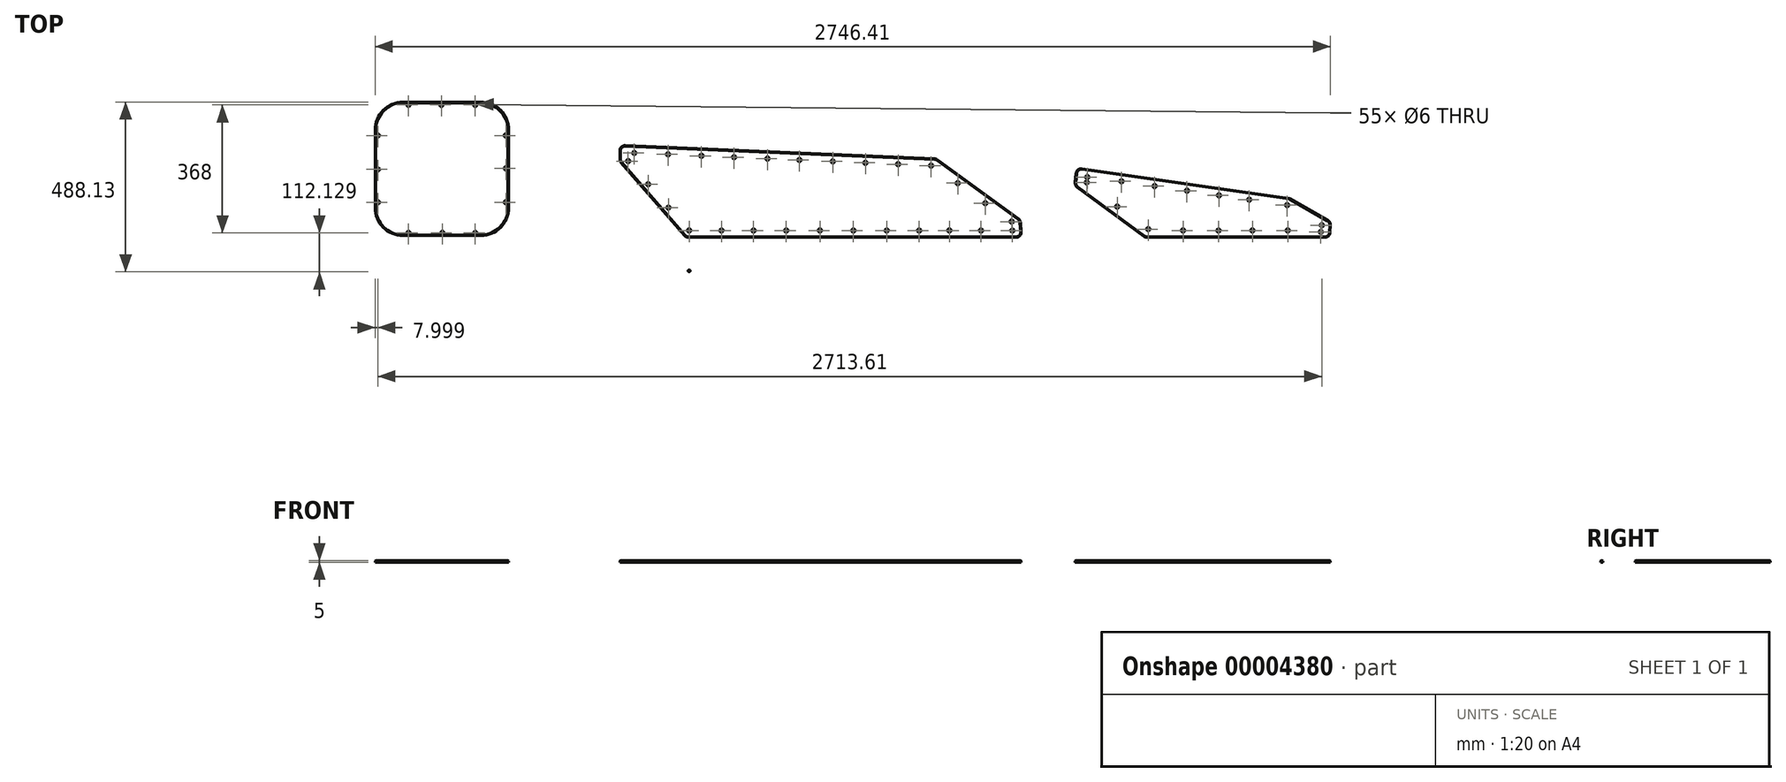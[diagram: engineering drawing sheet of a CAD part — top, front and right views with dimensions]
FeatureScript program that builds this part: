
annotation { "Feature Type Name" : "Feature", "Feature Type Description" : "" }
export const myFeature = defineFeature(function(context is Context, id is Id, definition is map)
    precondition{}
    {
        {
            var Q0;
            Q0=qCreatedBy(makeId("Top.planeOp"),FACE);
            var sketch = newSketch(context, id + "F0", { "sketchPlane" : qUnion([Q0])});
            skLineSegment(sketch, "E0", {"start": v(-249.6, -64.7) * mm, "end": v(262.12, -64.7) * mm});
            skLineSegment(sketch, "E1", {"start": v(277.1, -50.37) * mm, "end": v(278.06, -28.88) * mm});
            skLineSegment(sketch, "E2", {"start": v(270.54, -15.2) * mm, "end": v(163.96, 45.87) * mm});
            skLineSegment(sketch, "E3", {"start": v(158.63, 47.7) * mm, "end": v(-436, 133.07) * mm});
            skLineSegment(sketch, "E4", {"start": v(-453.05, 119.68) * mm, "end": v(-455.69, 92.78) * mm});
            skLineSegment(sketch, "E5", {"start": v(-449.66, 79.24) * mm, "end": v(-258.5, -61.77) * mm});
            skCircle(sketch, "E6", {"center": v(-420.96, 108.82) * mm, "radius": 3 * mm});
            skCircle(sketch, "E7", {"center": v(-422.47, 93.47) * mm, "radius": 3 * mm});
            skCircle(sketch, "E8", {"center": v(-322.71, 96.71) * mm, "radius": 3 * mm});
            skCircle(sketch, "E9", {"center": v(-334.84, 23.85) * mm, "radius": 3 * mm});
            skCircle(sketch, "E10", {"center": v(-245.64, -40.7) * mm, "radius": 3 * mm});
            skCircle(sketch, "E11", {"center": v(-145.53, -44.7) * mm, "radius": 3 * mm});
            skCircle(sketch, "E12", {"center": v(-43.53, -44.7) * mm, "radius": 3 * mm});
            skCircle(sketch, "E13", {"center": v(53.97, -44.7) * mm, "radius": 3 * mm});
            skCircle(sketch, "E14", {"center": v(155.47, -44.7) * mm, "radius": 3 * mm});
            skCircle(sketch, "E15", {"center": v(250.47, -48.7) * mm, "radius": 3 * mm});
            skCircle(sketch, "E16", {"center": v(253.28, -29.52) * mm, "radius": 3 * mm});
            skCircle(sketch, "E17", {"center": v(153.67, 28.21) * mm, "radius": 3 * mm});
            skCircle(sketch, "E18", {"center": v(44.8, 43.87) * mm, "radius": 3 * mm});
            skCircle(sketch, "E19", {"center": v(-42.3, 56.4) * mm, "radius": 3 * mm});
            skCircle(sketch, "E20", {"center": v(-134.36, 69.63) * mm, "radius": 3 * mm});
            skCircle(sketch, "E21", {"center": v(-227.4, 83) * mm, "radius": 3 * mm});
            skLineSegment(sketch, "E22", {"start": v(-625.64, -64.7) * mm, "end": v(-1567.54, -64.7) * mm});
            skLineSegment(sketch, "E23", {"start": v(-1578.88, -59.52) * mm, "end": v(-1761.2, 151.07) * mm});
            skLineSegment(sketch, "E24", {"start": v(-1764.87, 160.89) * mm, "end": v(-1764.87, 184.64) * mm});
            skLineSegment(sketch, "E25", {"start": v(-1749.23, 199.63) * mm, "end": v(-859.52, 161.5) * mm});
            skLineSegment(sketch, "E26", {"start": v(-851.32, 158.63) * mm, "end": v(-618.96, -10.8) * mm});
            skLineSegment(sketch, "E27", {"start": v(-612.84, -21.73) * mm, "end": v(-610.7, -48.5) * mm});
            skLineSegment(sketch, "E28", {"start": v(-613.21, -17.1) * mm, "end": v(-613.95, -17.16) * mm});
            skCircle(sketch, "E29", {"center": v(-1723.05, 178.36) * mm, "radius": 3 * mm});
            skCircle(sketch, "E30", {"center": v(-1740.97, 154.78) * mm, "radius": 3 * mm});
            skCircle(sketch, "E31", {"center": v(-1683.36, 88.25) * mm, "radius": 3 * mm});
            skCircle(sketch, "E32", {"center": v(-1626.14, 174.22) * mm, "radius": 3 * mm});
            skCircle(sketch, "E33", {"center": v(-1530.23, 170.13) * mm, "radius": 3 * mm});
            skCircle(sketch, "E34", {"center": v(-1436.31, 166.11) * mm, "radius": 3 * mm});
            skCircle(sketch, "E35", {"center": v(-1625.1, 20.97) * mm, "radius": 3 * mm});
            skCircle(sketch, "E36", {"center": v(-1565.4, -44.7) * mm, "radius": 3 * mm});
            skCircle(sketch, "E37", {"center": v(-1472.4, -44.7) * mm, "radius": 3 * mm});
            skCircle(sketch, "E38", {"center": v(-1380.4, -44.7) * mm, "radius": 3 * mm});
            skCircle(sketch, "E39", {"center": v(-1340.4, 162.02) * mm, "radius": 3 * mm});
            skCircle(sketch, "E40", {"center": v(-1248.48, 158.1) * mm, "radius": 3 * mm});
            skCircle(sketch, "E41", {"center": v(-1286.4, -44.7) * mm, "radius": 3 * mm});
            skCircle(sketch, "E42", {"center": v(-1189.4, -44.7) * mm, "radius": 3 * mm});
            skCircle(sketch, "E43", {"center": v(-1152.57, 154) * mm, "radius": 3 * mm});
            skCircle(sketch, "E44", {"center": v(-1058.66, 149.98) * mm, "radius": 3 * mm});
            skCircle(sketch, "E45", {"center": v(-1093.4, -44.7) * mm, "radius": 3 * mm});
            skCircle(sketch, "E46", {"center": v(-997.4, -44.7) * mm, "radius": 3 * mm});
            skCircle(sketch, "E47", {"center": v(-964.74, 145.97) * mm, "radius": 3 * mm});
            skCircle(sketch, "E48", {"center": v(-869.83, 141.91) * mm, "radius": 3 * mm});
            skCircle(sketch, "E49", {"center": v(-904.4, -44.7) * mm, "radius": 3 * mm});
            skCircle(sketch, "E50", {"center": v(-793.24, 91.52) * mm, "radius": 3 * mm});
            skCircle(sketch, "E51", {"center": v(-817.4, -44.7) * mm, "radius": 3 * mm});
            skCircle(sketch, "E52", {"center": v(-714.06, 33.79) * mm, "radius": 3 * mm});
            skCircle(sketch, "E53", {"center": v(-726.4, -44.7) * mm, "radius": 3 * mm});
            skCircle(sketch, "E54", {"center": v(-638.13, -19.1) * mm, "radius": 3 * mm});
            skCircle(sketch, "E55", {"center": v(-636.4, -44.7) * mm, "radius": 3 * mm});
            skPoint(sketch, "E56.visualSharp", {"position": v(-1574.4, -64.7) * mm});
            skArc(sketch, "E56.filletArc", {"start": v(-1578.88, -59.52) * mm, "mid": v(-1573.77, -63.35) * mm, "end": v(-1567.54, -64.7) * mm});
            skPoint(sketch, "E57.visualSharp", {"position": v(-1764.87, 155.3) * mm});
            skArc(sketch, "E57.filletArc", {"start": v(-1764.87, 160.89) * mm, "mid": v(-1763.92, 155.65) * mm, "end": v(-1761.2, 151.07) * mm});
            skPoint(sketch, "E58.visualSharp", {"position": v(-1764.87, 200.3) * mm});
            skArc(sketch, "E58.filletArc", {"start": v(-1749.23, 199.63) * mm, "mid": v(-1760.24, 195.47) * mm, "end": v(-1764.87, 184.64) * mm});
            skPoint(sketch, "E59.visualSharp", {"position": v(-854.99, 161.3) * mm});
            skArc(sketch, "E59.filletArc", {"start": v(-851.32, 158.63) * mm, "mid": v(-855.2, 160.66) * mm, "end": v(-859.52, 161.5) * mm});
            skPoint(sketch, "E60.visualSharp", {"position": v(-613.4, -14.86) * mm});
            skArc(sketch, "E60.filletArc", {"start": v(-612.84, -21.73) * mm, "mid": v(-614.7, -15.6) * mm, "end": v(-618.96, -10.8) * mm});
            skPoint(sketch, "E61.visualSharp", {"position": v(-609.4, -64.7) * mm});
            skArc(sketch, "E61.filletArc", {"start": v(-625.64, -64.7) * mm, "mid": v(-614.62, -59.88) * mm, "end": v(-610.7, -48.5) * mm});
            skPoint(sketch, "E62.visualSharp", {"position": v(-451.52, 135.3) * mm});
            skArc(sketch, "E62.filletArc", {"start": v(-436, 133.07) * mm, "mid": v(-447.38, 130.02) * mm, "end": v(-453.05, 119.68) * mm});
            skPoint(sketch, "E63.visualSharp", {"position": v(-456.52, 84.3) * mm});
            skArc(sketch, "E63.filletArc", {"start": v(-455.69, 92.78) * mm, "mid": v(-454.46, 85.21) * mm, "end": v(-449.66, 79.24) * mm});
            skPoint(sketch, "E64.visualSharp", {"position": v(-254.53, -64.7) * mm});
            skArc(sketch, "E64.filletArc", {"start": v(-258.5, -61.77) * mm, "mid": v(-254.28, -63.95) * mm, "end": v(-249.6, -64.7) * mm});
            skPoint(sketch, "E65.visualSharp", {"position": v(276.47, -64.7) * mm});
            skArc(sketch, "E65.filletArc", {"start": v(262.12, -64.7) * mm, "mid": v(272.5, -60.54) * mm, "end": v(277.1, -50.37) * mm});
            skPoint(sketch, "E66.visualSharp", {"position": v(278.47, -19.75) * mm});
            skArc(sketch, "E66.filletArc", {"start": v(278.06, -28.88) * mm, "mid": v(276.22, -20.98) * mm, "end": v(270.54, -15.2) * mm});
            skPoint(sketch, "E67.visualSharp", {"position": v(161.47, 47.3) * mm});
            skArc(sketch, "E67.filletArc", {"start": v(163.96, 45.87) * mm, "mid": v(161.38, 47.04) * mm, "end": v(158.63, 47.7) * mm});
            skCircle(sketch, "E68.0.MirrorC", {"center": v(-1565.4, -160.65) * mm, "radius": 3 * mm});
            skCircle(sketch, "E68.1.MirrorC", {"center": v(-1740.97, -360.13) * mm, "radius": 3 * mm});
            skArc(sketch, "E68.2.MirrorCS", {"start": v(-612.84, -183.63) * mm, "mid": v(-614.7, -189.75) * mm, "end": v(-618.96, -194.55) * mm});
            skArc(sketch, "E68.3.MirrorCS", {"start": v(-1764.87, -366.24) * mm, "mid": v(-1763.92, -361) * mm, "end": v(-1761.2, -356.42) * mm});
            skArc(sketch, "E68.4.MirrorCS", {"start": v(-851.32, -363.98) * mm, "mid": v(-855.2, -366.02) * mm, "end": v(-859.52, -366.84) * mm});
            skArc(sketch, "E68.5.MirrorCS", {"start": v(-1578.88, -145.83) * mm, "mid": v(-1573.77, -142) * mm, "end": v(-1567.54, -140.65) * mm});
            skCircle(sketch, "E68.6.MirrorC", {"center": v(-714.06, -239.14) * mm, "radius": 3 * mm});
            skCircle(sketch, "E68.7.MirrorC", {"center": v(-793.24, -296.88) * mm, "radius": 3 * mm});
            skCircle(sketch, "E68.8.MirrorC", {"center": v(-636.4, -160.65) * mm, "radius": 3 * mm});
            skCircle(sketch, "E68.9.MirrorC", {"center": v(-1472.4, -160.65) * mm, "radius": 3 * mm});
            skLineSegment(sketch, "E68.10.MirrorCS", {"start": v(-1764.87, -366.24) * mm, "end": v(-1764.87, -390) * mm});
            skCircle(sketch, "E68.11.MirrorC", {"center": v(-964.74, -351.32) * mm, "radius": 3 * mm});
            skCircle(sketch, "E68.12.MirrorC", {"center": v(-1683.36, -293.6) * mm, "radius": 3 * mm});
            skCircle(sketch, "E68.13.MirrorC", {"center": v(-997.4, -160.65) * mm, "radius": 3 * mm});
            skCircle(sketch, "E68.14.MirrorC", {"center": v(-1093.4, -160.65) * mm, "radius": 3 * mm});
            skCircle(sketch, "E68.15.MirrorC", {"center": v(-1340.4, -367.37) * mm, "radius": 3 * mm});
            skArc(sketch, "E68.16.MirrorCS", {"start": v(-1749.23, -404.98) * mm, "mid": v(-1760.24, -400.82) * mm, "end": v(-1764.87, -390) * mm});
            skCircle(sketch, "E68.17.MirrorC", {"center": v(-904.4, -160.65) * mm, "radius": 3 * mm});
            skCircle(sketch, "E68.18.MirrorC", {"center": v(-1625.1, -226.32) * mm, "radius": 3 * mm});
            skCircle(sketch, "E68.19.MirrorC", {"center": v(-1189.4, -160.65) * mm, "radius": 3 * mm});
            skCircle(sketch, "E68.20.MirrorC", {"center": v(-1286.4, -160.65) * mm, "radius": 3 * mm});
            skCircle(sketch, "E68.21.MirrorC", {"center": v(-1723.05, -383.72) * mm, "radius": 3 * mm});
            skCircle(sketch, "E68.22.MirrorC", {"center": v(-1380.4, -160.65) * mm, "radius": 3 * mm});
            skCircle(sketch, "E68.23.MirrorC", {"center": v(-817.4, -160.65) * mm, "radius": 3 * mm});
            skCircle(sketch, "E68.24.MirrorC", {"center": v(-869.83, -347.27) * mm, "radius": 3 * mm});
            skCircle(sketch, "E68.25.MirrorC", {"center": v(-638.13, -186.25) * mm, "radius": 3 * mm});
            skCircle(sketch, "E68.26.MirrorC", {"center": v(-1436.31, -371.47) * mm, "radius": 3 * mm});
            skCircle(sketch, "E68.27.MirrorC", {"center": v(-1530.23, -375.48) * mm, "radius": 3 * mm});
            skArc(sketch, "E68.28.MirrorCS", {"start": v(-625.64, -140.65) * mm, "mid": v(-614.62, -145.48) * mm, "end": v(-610.7, -156.85) * mm});
            skCircle(sketch, "E68.29.MirrorC", {"center": v(-1626.14, -379.58) * mm, "radius": 3 * mm});
            skCircle(sketch, "E68.30.MirrorC", {"center": v(-1058.66, -355.33) * mm, "radius": 3 * mm});
            skCircle(sketch, "E68.31.MirrorC", {"center": v(-726.4, -160.65) * mm, "radius": 3 * mm});
            skCircle(sketch, "E68.32.MirrorC", {"center": v(-1248.48, -363.44) * mm, "radius": 3 * mm});
            skLineSegment(sketch, "E68.33.MirrorCS", {"start": v(-612.84, -183.63) * mm, "end": v(-610.7, -156.85) * mm});
            skCircle(sketch, "E68.34.MirrorC", {"center": v(-1152.57, -359.34) * mm, "radius": 3 * mm});
            skPoint(sketch, "E68.35.MirrorP", {"position": v(-609.4, -140.65) * mm});
            skLineSegment(sketch, "E68.36.MirrorCS", {"start": v(-1578.88, -145.83) * mm, "end": v(-1761.2, -356.42) * mm});
            skPoint(sketch, "E68.37.MirrorP", {"position": v(-1764.87, -360.65) * mm});
            skPoint(sketch, "E68.38.MirrorP", {"position": v(-1574.4, -140.65) * mm});
            skPoint(sketch, "E68.39.MirrorP", {"position": v(-1764.87, -405.65) * mm});
            skPoint(sketch, "E68.40.MirrorP", {"position": v(-613.4, -190.49) * mm});
            skPoint(sketch, "E68.41.MirrorP", {"position": v(-854.99, -366.65) * mm});
            skLineSegment(sketch, "E68.42.MirrorCS", {"start": v(-851.32, -363.98) * mm, "end": v(-618.96, -194.55) * mm});
            skLineSegment(sketch, "E68.43.MirrorCS", {"start": v(-1749.23, -404.98) * mm, "end": v(-859.52, -366.84) * mm});
            skLineSegment(sketch, "E68.44.MirrorCS", {"start": v(-625.64, -140.65) * mm, "end": v(-1567.54, -140.65) * mm});
            skArc(sketch, "E69.0.MirrorCS", {"start": v(278.06, -176.47) * mm, "mid": v(276.22, -184.37) * mm, "end": v(270.54, -190.15) * mm});
            skArc(sketch, "E69.1.MirrorCS", {"start": v(163.96, -251.22) * mm, "mid": v(161.38, -252.4) * mm, "end": v(158.63, -253.06) * mm});
            skArc(sketch, "E69.2.MirrorCS", {"start": v(-258.5, -143.58) * mm, "mid": v(-254.28, -141.4) * mm, "end": v(-249.6, -140.65) * mm});
            skCircle(sketch, "E69.3.MirrorC", {"center": v(153.67, -233.56) * mm, "radius": 3 * mm});
            skCircle(sketch, "E69.4.MirrorC", {"center": v(-145.53, -160.65) * mm, "radius": 3 * mm});
            skCircle(sketch, "E69.5.MirrorC", {"center": v(-334.84, -229.2) * mm, "radius": 3 * mm});
            skCircle(sketch, "E69.6.MirrorC", {"center": v(-43.53, -160.65) * mm, "radius": 3 * mm});
            skArc(sketch, "E69.7.MirrorCS", {"start": v(262.12, -140.65) * mm, "mid": v(272.5, -144.8) * mm, "end": v(277.1, -154.98) * mm});
            skCircle(sketch, "E69.8.MirrorC", {"center": v(-134.36, -274.98) * mm, "radius": 3 * mm});
            skCircle(sketch, "E69.9.MirrorC", {"center": v(-322.71, -302.07) * mm, "radius": 3 * mm});
            skCircle(sketch, "E69.10.MirrorC", {"center": v(253.28, -175.84) * mm, "radius": 3 * mm});
            skCircle(sketch, "E69.11.MirrorC", {"center": v(155.47, -160.65) * mm, "radius": 3 * mm});
            skArc(sketch, "E69.12.MirrorCS", {"start": v(-455.69, -298.13) * mm, "mid": v(-454.46, -290.56) * mm, "end": v(-449.66, -284.6) * mm});
            skCircle(sketch, "E69.13.MirrorC", {"center": v(44.8, -249.22) * mm, "radius": 3 * mm});
            skArc(sketch, "E69.14.MirrorCS", {"start": v(-436, -338.42) * mm, "mid": v(-447.38, -335.37) * mm, "end": v(-453.05, -325.04) * mm});
            skCircle(sketch, "E69.15.MirrorC", {"center": v(-420.96, -314.17) * mm, "radius": 3 * mm});
            skCircle(sketch, "E69.16.MirrorC", {"center": v(53.97, -160.65) * mm, "radius": 3 * mm});
            skCircle(sketch, "E69.17.MirrorC", {"center": v(-245.64, -164.65) * mm, "radius": 3 * mm});
            skCircle(sketch, "E69.18.MirrorC", {"center": v(-422.47, -298.82) * mm, "radius": 3 * mm});
            skLineSegment(sketch, "E69.19.MirrorCS", {"start": v(277.1, -154.98) * mm, "end": v(278.06, -176.47) * mm});
            skCircle(sketch, "E69.20.MirrorC", {"center": v(-42.3, -261.75) * mm, "radius": 3 * mm});
            skCircle(sketch, "E69.21.MirrorC", {"center": v(250.47, -156.65) * mm, "radius": 3 * mm});
            skCircle(sketch, "E69.22.MirrorC", {"center": v(-227.4, -288.36) * mm, "radius": 3 * mm});
            skPoint(sketch, "E69.23.MirrorP", {"position": v(-456.52, -289.65) * mm});
            skPoint(sketch, "E69.24.MirrorP", {"position": v(278.47, -185.6) * mm});
            skLineSegment(sketch, "E69.25.MirrorCS", {"start": v(-449.66, -284.6) * mm, "end": v(-258.5, -143.58) * mm});
            skPoint(sketch, "E69.26.MirrorP", {"position": v(161.47, -252.65) * mm});
            skLineSegment(sketch, "E69.27.MirrorCS", {"start": v(-249.6, -140.65) * mm, "end": v(262.12, -140.65) * mm});
            skLineSegment(sketch, "E69.28.MirrorCS", {"start": v(-453.05, -325.04) * mm, "end": v(-455.69, -298.13) * mm});
            skPoint(sketch, "E69.29.MirrorP", {"position": v(-254.53, -140.65) * mm});
            skPoint(sketch, "E69.30.MirrorP", {"position": v(276.47, -140.65) * mm});
            skLineSegment(sketch, "E69.31.MirrorCS", {"start": v(270.54, -190.15) * mm, "end": v(163.96, -251.22) * mm});
            skPoint(sketch, "E69.32.MirrorP", {"position": v(-451.52, -340.65) * mm});
            skLineSegment(sketch, "E69.33.MirrorCS", {"start": v(158.63, -253.06) * mm, "end": v(-436, -338.42) * mm});
            skSolve(sketch);
        }
        {
            var Q0;
            Q0=qCreatedBy(makeId("Top.planeOp"),FACE);
            var sketch = newSketch(context, id + "F1", { "sketchPlane" : qUnion([Q0])});
            skLineSegment(sketch, "E70.bottom", {"start": v(-2388.33, 324.48) * mm, "end": v(-2164.33, 324.48) * mm});
            skLineSegment(sketch, "E70.top", {"start": v(-2388.33, -59.52) * mm, "end": v(-2164.33, -59.52) * mm});
            skLineSegment(sketch, "E70.left", {"start": v(-2468.33, 244.48) * mm, "end": v(-2468.33, 20.48) * mm});
            skLineSegment(sketch, "E70.right", {"start": v(-2084.33, 244.48) * mm, "end": v(-2084.33, 20.48) * mm});
            skCircle(sketch, "E71", {"center": v(-2277.81, 316.48) * mm, "radius": 3 * mm});
            skLineSegment(sketch, "E72", {"start": v(-2372.33, 324.48) * mm, "end": v(-2372.33, 316.48) * mm});
            skLineSegment(sketch, "E73", {"start": v(-2180.33, 324.48) * mm, "end": v(-2180.33, 316.48) * mm});
            skLineSegment(sketch, "E74", {"start": v(-2276.33, 324.48) * mm, "end": v(-2372.33, 324.48) * mm});
            skLineSegment(sketch, "E75", {"start": v(-2276.33, 324.48) * mm, "end": v(-2180.33, 324.48) * mm});
            skCircle(sketch, "E76", {"center": v(-2372.33, 316.48) * mm, "radius": 3 * mm});
            skCircle(sketch, "E77", {"center": v(-2180.33, 316.48) * mm, "radius": 3 * mm});
            skPoint(sketch, "E78", {"position": v(-2276.33, 132.48) * mm});
            skCircle(sketch, "E79.1.0", {"center": v(918.18, -2210.93) * mm, "radius": 3 * mm});
            skCircle(sketch, "E79.1.1", {"center": v(870.18, -2127.8) * mm, "radius": 3 * mm});
            skCircle(sketch, "E79.1.2", {"center": v(822.18, -2044.66) * mm, "radius": 3 * mm});
            skPoint(sketch, "E79.1.3", {"position": v(1029.96, -2035.54) * mm});
            skCircle(sketch, "E79.2.0", {"center": v(1455.63, 1900.63) * mm, "radius": 3 * mm});
            skCircle(sketch, "E79.2.1", {"center": v(1407.63, 1817.5) * mm, "radius": 3 * mm});
            skCircle(sketch, "E79.2.2", {"center": v(1359.63, 1734.36) * mm, "radius": 3 * mm});
            skPoint(sketch, "E79.2.3", {"position": v(1247.85, 1909.75) * mm});
            skPoint(sketch, "E79.center", {"position": v(0, 0) * mm});
            skCircle(sketch, "E80.1.0", {"center": v(-2460.33, 36.48) * mm, "radius": 3 * mm});
            skCircle(sketch, "E80.1.1", {"center": v(-2460.33, 131) * mm, "radius": 3 * mm});
            skCircle(sketch, "E80.1.2", {"center": v(-2460.33, 228.48) * mm, "radius": 3 * mm});
            skCircle(sketch, "E80.2.0", {"center": v(-2180.33, -51.52) * mm, "radius": 3 * mm});
            skCircle(sketch, "E80.2.1", {"center": v(-2274.85, -51.52) * mm, "radius": 3 * mm});
            skCircle(sketch, "E80.2.2", {"center": v(-2372.33, -51.52) * mm, "radius": 3 * mm});
            skCircle(sketch, "E80.3.0", {"center": v(-2092.33, 228.48) * mm, "radius": 3 * mm});
            skCircle(sketch, "E80.3.1", {"center": v(-2092.33, 133.96) * mm, "radius": 3 * mm});
            skCircle(sketch, "E80.3.2", {"center": v(-2092.33, 36.48) * mm, "radius": 3 * mm});
            skPoint(sketch, "E81.visualSharp", {"position": v(-2468.33, 324.48) * mm});
            skArc(sketch, "E81.filletArc", {"start": v(-2388.33, 324.48) * mm, "mid": v(-2444.9, 301.05) * mm, "end": v(-2468.33, 244.48) * mm});
            skPoint(sketch, "E82.visualSharp", {"position": v(-2084.33, 324.48) * mm});
            skArc(sketch, "E82.filletArc", {"start": v(-2084.33, 244.48) * mm, "mid": v(-2107.76, 301.05) * mm, "end": v(-2164.33, 324.48) * mm});
            skPoint(sketch, "E83.visualSharp", {"position": v(-2084.33, -59.52) * mm});
            skArc(sketch, "E83.filletArc", {"start": v(-2164.33, -59.52) * mm, "mid": v(-2107.76, -36.09) * mm, "end": v(-2084.33, 20.48) * mm});
            skPoint(sketch, "E84.visualSharp", {"position": v(-2468.33, -59.52) * mm});
            skArc(sketch, "E84.filletArc", {"start": v(-2468.33, 20.48) * mm, "mid": v(-2444.9, -36.09) * mm, "end": v(-2388.33, -59.52) * mm});
            skPoint(sketch, "E85", {"position": v(-2468.33, 132.48) * mm});
            skPoint(sketch, "E86", {"position": v(-2276.33, -59.52) * mm});
            skSolve(sketch);
        }
        {
            var Q0;
            Q0=makeQuery(id+"F1.imprint","IMPRINT",FACE,{"disambiguationData":[TD([[makeQuery(id+"F1.imprint","IMPRINT",EDGE,{"derivedFrom":sQuery(id+"F1.wireOp",EDGE,"E70.top")}),1.0]])]});
            var Q1;
            Q1=makeQuery(id+"F0.imprint","IMPRINT",FACE,{"disambiguationData":[TD([[makeQuery(id+"F0.imprint","IMPRINT",EDGE,{"derivedFrom":sQuery(id+"F0.wireOp",EDGE,"E22")}),-1.0]])]});
            var Q2;
            Q2=makeQuery(id+"F0.imprint","IMPRINT",FACE,{"disambiguationData":[TD([[makeQuery(id+"F0.imprint","IMPRINT",EDGE,{"derivedFrom":sQuery(id+"F0.wireOp",EDGE,"E0")}),1.0]])]});
            var Q3;
            Q3=makeQuery(id+"F0.imprint","IMPRINT",FACE,{"disambiguationData":[TD([[makeQuery(id+"F0.imprint","IMPRINT",EDGE,{"derivedFrom":sQuery(id+"F0.wireOp",EDGE,"E69.0.MirrorCS")}),-1.0]])]});
            var Q4;
            Q4=makeQuery(id+"F0.imprint","IMPRINT",FACE,{"disambiguationData":[TD([[makeQuery(id+"F0.imprint","IMPRINT",EDGE,{"derivedFrom":sQuery(id+"F0.wireOp",EDGE,"E68.0.MirrorC")}),1.0]])]});
            extrude(context, id + "F2", {"entities" : qUnion([Q0, Q1, Q2, Q3, Q4]), "depth" : 5 * mm});
        }
        {
            var Q0;
            Q0=makeQuery(id+"F2.opExtrude","CAP_FACE",FACE,{"disambiguationData":[OSD([sQuery(id+"F1.wireOp",EDGE,"E70.bottom"),sQuery(id+"F1.wireOp",EDGE,"E70.top"),sQuery(id+"F1.wireOp",EDGE,"E70.left"),sQuery(id+"F1.wireOp",EDGE,"E70.right"),sQuery(id+"F1.wireOp",EDGE,"E71"),sQuery(id+"F1.wireOp",EDGE,"E75"),sQuery(id+"F1.wireOp",EDGE,"E76"),sQuery(id+"F1.wireOp",EDGE,"E77"),sQuery(id+"F1.wireOp",EDGE,"E80.1.0"),sQuery(id+"F1.wireOp",EDGE,"E80.1.1"),sQuery(id+"F1.wireOp",EDGE,"E80.1.2"),sQuery(id+"F1.wireOp",EDGE,"E80.2.0"),sQuery(id+"F1.wireOp",EDGE,"E80.2.1"),sQuery(id+"F1.wireOp",EDGE,"E80.2.2"),sQuery(id+"F1.wireOp",EDGE,"E80.3.0"),sQuery(id+"F1.wireOp",EDGE,"E80.3.1"),sQuery(id+"F1.wireOp",EDGE,"E80.3.2"),sQuery(id+"F1.wireOp",EDGE,"E81.filletArc"),sQuery(id+"F1.wireOp",EDGE,"E82.filletArc"),sQuery(id+"F1.wireOp",EDGE,"E83.filletArc"),sQuery(id+"F1.wireOp",EDGE,"E84.filletArc")])],"isStart":false});
            var Q1;
            Q1=makeQuery(id+"F2.opExtrude","CAP_FACE",FACE,{"disambiguationData":[OSD([sQuery(id+"F0.wireOp",EDGE,"E22"),sQuery(id+"F0.wireOp",EDGE,"E23"),sQuery(id+"F0.wireOp",EDGE,"E24"),sQuery(id+"F0.wireOp",EDGE,"E25"),sQuery(id+"F0.wireOp",EDGE,"E26"),sQuery(id+"F0.wireOp",EDGE,"E27"),sQuery(id+"F0.wireOp",EDGE,"E29"),sQuery(id+"F0.wireOp",EDGE,"E30"),sQuery(id+"F0.wireOp",EDGE,"E31"),sQuery(id+"F0.wireOp",EDGE,"E32"),sQuery(id+"F0.wireOp",EDGE,"E33"),sQuery(id+"F0.wireOp",EDGE,"E34"),sQuery(id+"F0.wireOp",EDGE,"E35"),sQuery(id+"F0.wireOp",EDGE,"E36"),sQuery(id+"F0.wireOp",EDGE,"E37"),sQuery(id+"F0.wireOp",EDGE,"E38"),sQuery(id+"F0.wireOp",EDGE,"E39"),sQuery(id+"F0.wireOp",EDGE,"E40"),sQuery(id+"F0.wireOp",EDGE,"E41"),sQuery(id+"F0.wireOp",EDGE,"E42"),sQuery(id+"F0.wireOp",EDGE,"E43"),sQuery(id+"F0.wireOp",EDGE,"E44"),sQuery(id+"F0.wireOp",EDGE,"E45"),sQuery(id+"F0.wireOp",EDGE,"E46"),sQuery(id+"F0.wireOp",EDGE,"E47"),sQuery(id+"F0.wireOp",EDGE,"E48"),sQuery(id+"F0.wireOp",EDGE,"E49"),sQuery(id+"F0.wireOp",EDGE,"E50"),sQuery(id+"F0.wireOp",EDGE,"E51"),sQuery(id+"F0.wireOp",EDGE,"E52"),sQuery(id+"F0.wireOp",EDGE,"E53"),sQuery(id+"F0.wireOp",EDGE,"E54"),sQuery(id+"F0.wireOp",EDGE,"E55"),sQuery(id+"F0.wireOp",EDGE,"E56.filletArc"),sQuery(id+"F0.wireOp",EDGE,"E57.filletArc"),sQuery(id+"F0.wireOp",EDGE,"E58.filletArc"),sQuery(id+"F0.wireOp",EDGE,"E59.filletArc"),sQuery(id+"F0.wireOp",EDGE,"E60.filletArc"),sQuery(id+"F0.wireOp",EDGE,"E61.filletArc")])],"isStart":false});
            var Q2;
            Q2=makeQuery(id+"F2.opExtrude","CAP_FACE",FACE,{"disambiguationData":[OSD([sQuery(id+"F0.wireOp",EDGE,"E0"),sQuery(id+"F0.wireOp",EDGE,"E1"),sQuery(id+"F0.wireOp",EDGE,"E2"),sQuery(id+"F0.wireOp",EDGE,"E3"),sQuery(id+"F0.wireOp",EDGE,"E4"),sQuery(id+"F0.wireOp",EDGE,"E5"),sQuery(id+"F0.wireOp",EDGE,"E6"),sQuery(id+"F0.wireOp",EDGE,"E7"),sQuery(id+"F0.wireOp",EDGE,"E8"),sQuery(id+"F0.wireOp",EDGE,"E9"),sQuery(id+"F0.wireOp",EDGE,"E10"),sQuery(id+"F0.wireOp",EDGE,"E11"),sQuery(id+"F0.wireOp",EDGE,"E12"),sQuery(id+"F0.wireOp",EDGE,"E13"),sQuery(id+"F0.wireOp",EDGE,"E14"),sQuery(id+"F0.wireOp",EDGE,"E15"),sQuery(id+"F0.wireOp",EDGE,"E16"),sQuery(id+"F0.wireOp",EDGE,"E17"),sQuery(id+"F0.wireOp",EDGE,"E18"),sQuery(id+"F0.wireOp",EDGE,"E19"),sQuery(id+"F0.wireOp",EDGE,"E20"),sQuery(id+"F0.wireOp",EDGE,"E21"),sQuery(id+"F0.wireOp",EDGE,"E62.filletArc"),sQuery(id+"F0.wireOp",EDGE,"E63.filletArc"),sQuery(id+"F0.wireOp",EDGE,"E64.filletArc"),sQuery(id+"F0.wireOp",EDGE,"E65.filletArc"),sQuery(id+"F0.wireOp",EDGE,"E66.filletArc"),sQuery(id+"F0.wireOp",EDGE,"E67.filletArc")])],"isStart":false});
            var Q3;
            Q3=makeQuery(id+"F2.opExtrude","CAP_FACE",FACE,{"disambiguationData":[OSD([sQuery(id+"F0.wireOp",EDGE,"E69.0.MirrorCS"),sQuery(id+"F0.wireOp",EDGE,"E69.1.MirrorCS"),sQuery(id+"F0.wireOp",EDGE,"E69.2.MirrorCS"),sQuery(id+"F0.wireOp",EDGE,"E69.3.MirrorC"),sQuery(id+"F0.wireOp",EDGE,"E69.4.MirrorC"),sQuery(id+"F0.wireOp",EDGE,"E69.5.MirrorC"),sQuery(id+"F0.wireOp",EDGE,"E69.6.MirrorC"),sQuery(id+"F0.wireOp",EDGE,"E69.7.MirrorCS"),sQuery(id+"F0.wireOp",EDGE,"E69.8.MirrorC"),sQuery(id+"F0.wireOp",EDGE,"E69.9.MirrorC"),sQuery(id+"F0.wireOp",EDGE,"E69.10.MirrorC"),sQuery(id+"F0.wireOp",EDGE,"E69.11.MirrorC"),sQuery(id+"F0.wireOp",EDGE,"E69.12.MirrorCS"),sQuery(id+"F0.wireOp",EDGE,"E69.13.MirrorC"),sQuery(id+"F0.wireOp",EDGE,"E69.14.MirrorCS"),sQuery(id+"F0.wireOp",EDGE,"E69.15.MirrorC"),sQuery(id+"F0.wireOp",EDGE,"E69.16.MirrorC"),sQuery(id+"F0.wireOp",EDGE,"E69.17.MirrorC"),sQuery(id+"F0.wireOp",EDGE,"E69.18.MirrorC"),sQuery(id+"F0.wireOp",EDGE,"E69.19.MirrorCS"),sQuery(id+"F0.wireOp",EDGE,"E69.20.MirrorC"),sQuery(id+"F0.wireOp",EDGE,"E69.21.MirrorC"),sQuery(id+"F0.wireOp",EDGE,"E69.22.MirrorC"),sQuery(id+"F0.wireOp",EDGE,"E69.25.MirrorCS"),sQuery(id+"F0.wireOp",EDGE,"E69.27.MirrorCS"),sQuery(id+"F0.wireOp",EDGE,"E69.28.MirrorCS"),sQuery(id+"F0.wireOp",EDGE,"E69.31.MirrorCS"),sQuery(id+"F0.wireOp",EDGE,"E69.33.MirrorCS")])],"isStart":false});
            var Q4;
            Q4=makeQuery(id+"F2.opExtrude","CAP_FACE",FACE,{"disambiguationData":[OSD([sQuery(id+"F0.wireOp",EDGE,"E68.0.MirrorC"),sQuery(id+"F0.wireOp",EDGE,"E68.1.MirrorC"),sQuery(id+"F0.wireOp",EDGE,"E68.2.MirrorCS"),sQuery(id+"F0.wireOp",EDGE,"E68.3.MirrorCS"),sQuery(id+"F0.wireOp",EDGE,"E68.4.MirrorCS"),sQuery(id+"F0.wireOp",EDGE,"E68.5.MirrorCS"),sQuery(id+"F0.wireOp",EDGE,"E68.6.MirrorC"),sQuery(id+"F0.wireOp",EDGE,"E68.7.MirrorC"),sQuery(id+"F0.wireOp",EDGE,"E68.8.MirrorC"),sQuery(id+"F0.wireOp",EDGE,"E68.9.MirrorC"),sQuery(id+"F0.wireOp",EDGE,"E68.10.MirrorCS"),sQuery(id+"F0.wireOp",EDGE,"E68.11.MirrorC"),sQuery(id+"F0.wireOp",EDGE,"E68.12.MirrorC"),sQuery(id+"F0.wireOp",EDGE,"E68.13.MirrorC"),sQuery(id+"F0.wireOp",EDGE,"E68.14.MirrorC"),sQuery(id+"F0.wireOp",EDGE,"E68.15.MirrorC"),sQuery(id+"F0.wireOp",EDGE,"E68.16.MirrorCS"),sQuery(id+"F0.wireOp",EDGE,"E68.17.MirrorC"),sQuery(id+"F0.wireOp",EDGE,"E68.18.MirrorC"),sQuery(id+"F0.wireOp",EDGE,"E68.19.MirrorC"),sQuery(id+"F0.wireOp",EDGE,"E68.20.MirrorC"),sQuery(id+"F0.wireOp",EDGE,"E68.21.MirrorC"),sQuery(id+"F0.wireOp",EDGE,"E68.22.MirrorC"),sQuery(id+"F0.wireOp",EDGE,"E68.23.MirrorC"),sQuery(id+"F0.wireOp",EDGE,"E68.24.MirrorC"),sQuery(id+"F0.wireOp",EDGE,"E68.25.MirrorC"),sQuery(id+"F0.wireOp",EDGE,"E68.26.MirrorC"),sQuery(id+"F0.wireOp",EDGE,"E68.27.MirrorC"),sQuery(id+"F0.wireOp",EDGE,"E68.28.MirrorCS"),sQuery(id+"F0.wireOp",EDGE,"E68.29.MirrorC"),sQuery(id+"F0.wireOp",EDGE,"E68.30.MirrorC"),sQuery(id+"F0.wireOp",EDGE,"E68.31.MirrorC"),sQuery(id+"F0.wireOp",EDGE,"E68.32.MirrorC"),sQuery(id+"F0.wireOp",EDGE,"E68.33.MirrorCS"),sQuery(id+"F0.wireOp",EDGE,"E68.34.MirrorC"),sQuery(id+"F0.wireOp",EDGE,"E68.36.MirrorCS"),sQuery(id+"F0.wireOp",EDGE,"E68.42.MirrorCS"),sQuery(id+"F0.wireOp",EDGE,"E68.43.MirrorCS"),sQuery(id+"F0.wireOp",EDGE,"E68.44.MirrorCS")])],"isStart":false});
            chamfer(context, id + "F3", {"entities" : qUnion([Q0, Q1, Q2, Q3, Q4]), "width" : 2 * mm, "tangentPropagation" : true});
        }
    });
